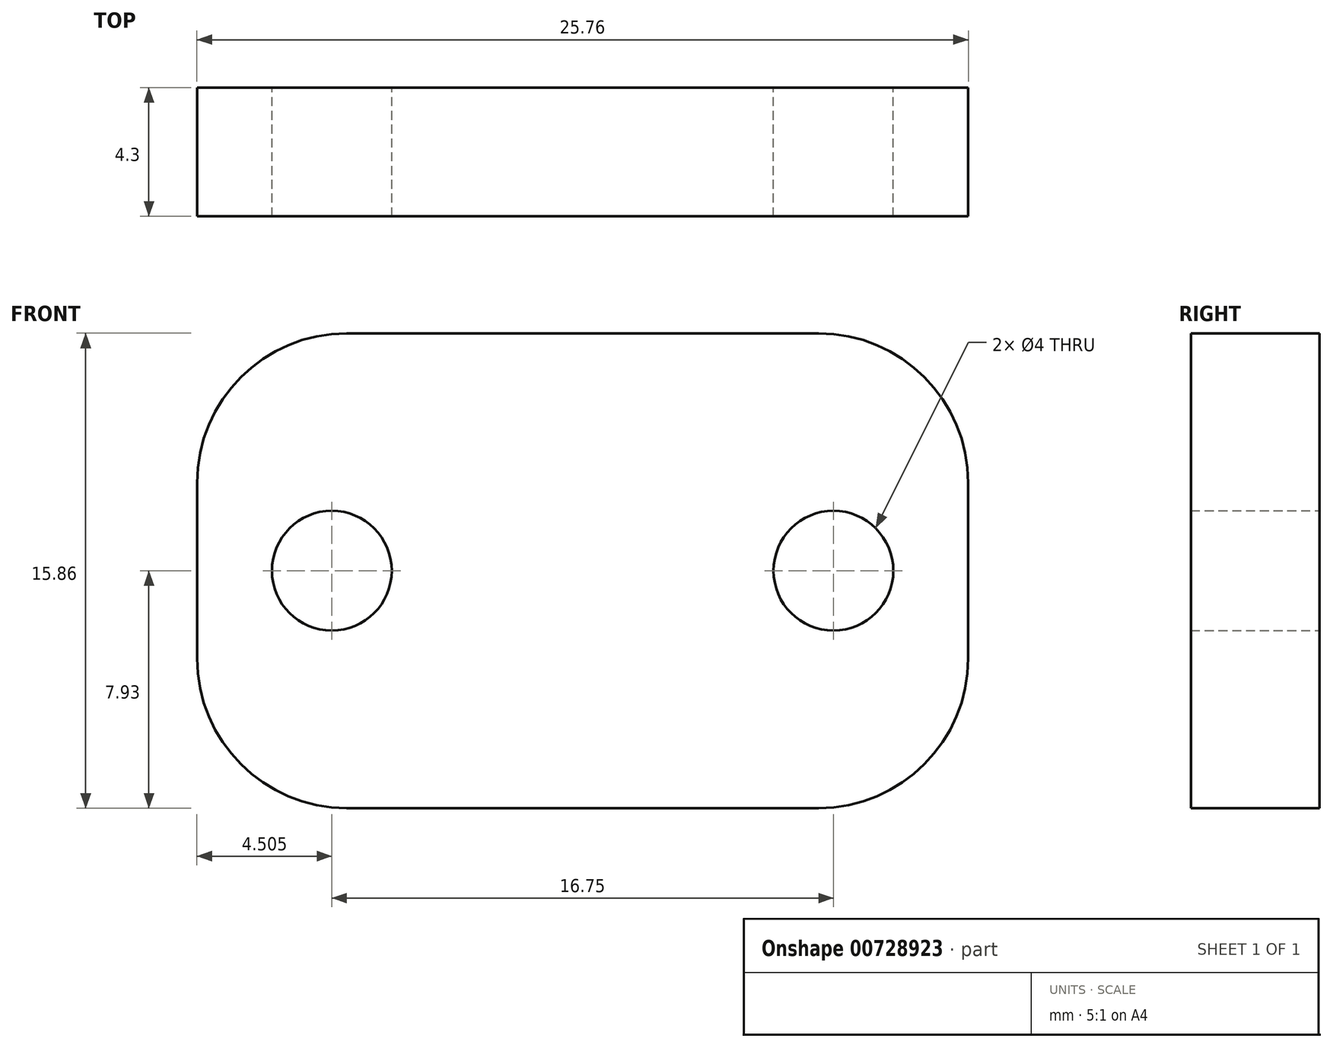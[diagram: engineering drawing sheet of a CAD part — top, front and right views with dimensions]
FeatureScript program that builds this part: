
annotation { "Feature Type Name" : "Feature", "Feature Type Description" : "" }
export const myFeature = defineFeature(function(context is Context, id is Id, definition is map)
    precondition{}
    {
        {
            var Q0;
            Q0=qCreatedBy(makeId("Front.planeOp"),FACE);
            var sketch = newSketch(context, id + "F0", { "sketchPlane" : qUnion([Q0])});
            skLineSegment(sketch, "E0.bottom", {"start": v(-7.88, 7.93) * mm, "end": v(7.88, 7.93) * mm});
            skLineSegment(sketch, "E0.top", {"start": v(-7.87, -7.92) * mm, "end": v(7.87, -7.92) * mm});
            skLineSegment(sketch, "E0.left", {"start": v(-12.88, 2.93) * mm, "end": v(-12.88, -2.92) * mm});
            skLineSegment(sketch, "E0.right", {"start": v(12.88, 2.93) * mm, "end": v(12.88, -2.93) * mm});
            skPoint(sketch, "E0.middle", {"position": v(0, 0) * mm});
            skPoint(sketch, "E1.visualSharp", {"position": v(12.88, 7.93) * mm});
            skArc(sketch, "E1.filletArc", {"start": v(12.88, 2.93) * mm, "mid": v(11.41, 6.46) * mm, "end": v(7.88, 7.93) * mm});
            skPoint(sketch, "E2.visualSharp", {"position": v(12.87, -7.92) * mm});
            skArc(sketch, "E2.filletArc", {"start": v(7.87, -7.93) * mm, "mid": v(11.41, -6.46) * mm, "end": v(12.88, -2.93) * mm});
            skPoint(sketch, "E3.visualSharp", {"position": v(-12.87, -7.92) * mm});
            skArc(sketch, "E3.filletArc", {"start": v(-12.88, -2.92) * mm, "mid": v(-11.41, -6.46) * mm, "end": v(-7.87, -7.92) * mm});
            skPoint(sketch, "E4.visualSharp", {"position": v(-12.88, 7.93) * mm});
            skArc(sketch, "E4.filletArc", {"start": v(-7.88, 7.93) * mm, "mid": v(-11.41, 6.46) * mm, "end": v(-12.88, 2.93) * mm});
            skCircle(sketch, "E5", {"center": v(8.38, 0) * mm, "radius": 2 * mm});
            skPoint(sketch, "E5.centerSnap0", {"position": v(12.88, 0) * mm});
            skCircle(sketch, "E6.MirrorC", {"center": v(-8.38, 0) * mm, "radius": 2 * mm});
            skSolve(sketch);
        }
        {
            var Q0;
            Q0 = qSketchRegion(id + "F0", true);
            extrude(context, id + "F1", {"entities" : qUnion([Q0]), "depth" : 4.3 * mm, "offsetDistance" : 25 * mm});
        }
    });
